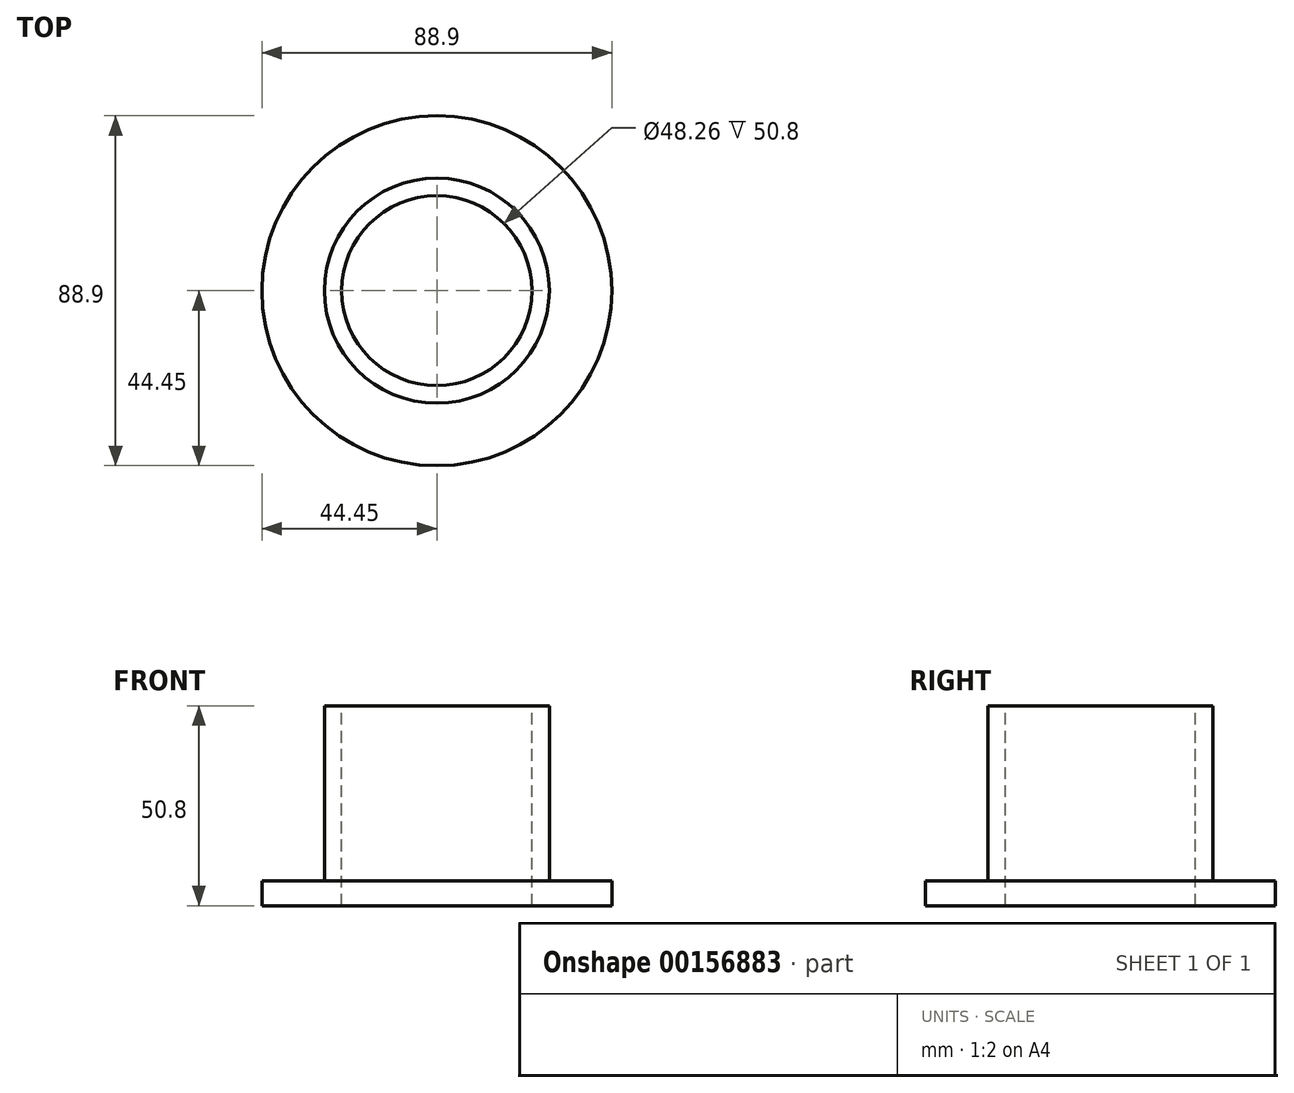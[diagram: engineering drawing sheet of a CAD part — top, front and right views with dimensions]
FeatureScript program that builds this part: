
annotation { "Feature Type Name" : "Feature", "Feature Type Description" : "" }
export const myFeature = defineFeature(function(context is Context, id is Id, definition is map)
    precondition{}
    {
        {
            var Q0;
            Q0=qCreatedBy(makeId("Front.planeOp"),FACE);
            var sketch = newSketch(context, id + "F0", { "sketchPlane" : qUnion([Q0])});
            skLineSegment(sketch, "E0", {"start": v(24.13, 50.8) * mm, "end": v(24.13, 0) * mm});
            skLineSegment(sketch, "E1", {"start": v(24.13, 0) * mm, "end": v(44.45, 0) * mm});
            skLineSegment(sketch, "E2", {"start": v(44.45, 0) * mm, "end": v(44.45, 6.35) * mm});
            skLineSegment(sketch, "E3", {"start": v(44.45, 6.35) * mm, "end": v(28.58, 6.35) * mm});
            skLineSegment(sketch, "E4", {"start": v(28.58, 6.35) * mm, "end": v(28.58, 50.8) * mm});
            skLineSegment(sketch, "E5", {"start": v(28.58, 50.8) * mm, "end": v(24.13, 50.8) * mm});
            skLineSegment(sketch, "E6", {"start": v(0, 70.47) * mm, "end": v(0, -29.05) * mm, "construction": true});
            skSolve(sketch);
        }
        {
            var Q0;
            Q0=makeQuery(id+"F0.imprint","IMPRINT",FACE,{"disambiguationData":[TD([[makeQuery(id+"F0.imprint","IMPRINT",EDGE,{"derivedFrom":sQuery(id+"F0.wireOp",EDGE,"E0")}),1.0]])]});
            var Q1;
            Q1=sQuery(id+"F0.wireOp",EDGE,"E6");
            revolve(context, id + "F1", {"entities" : qUnion([Q0]), "axis" : qUnion([Q1]), "revolveType" : RevolveType.FULL});
        }
    });
